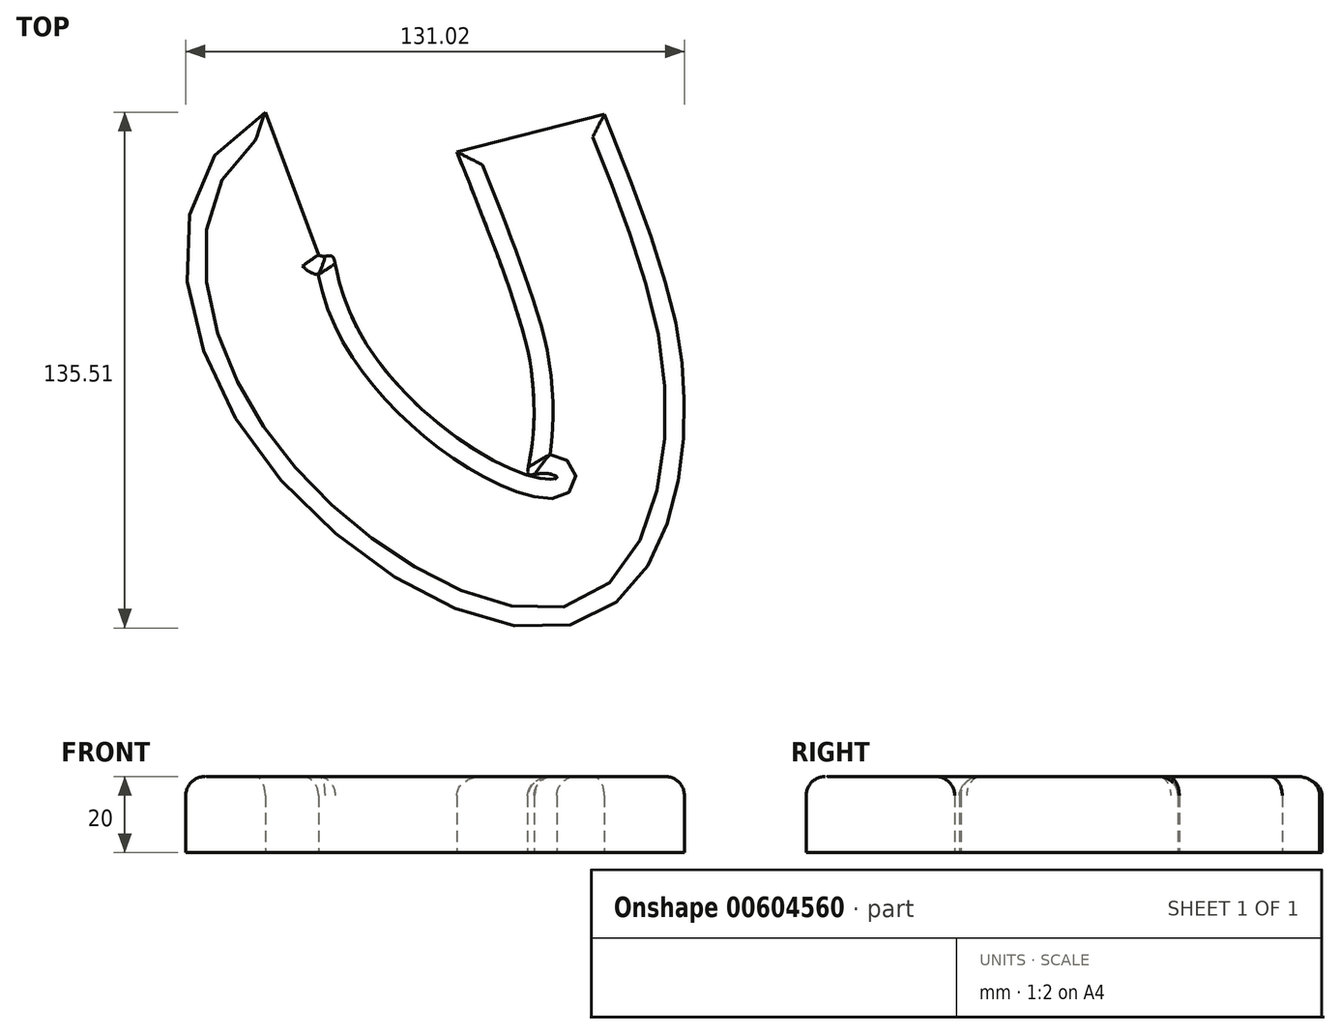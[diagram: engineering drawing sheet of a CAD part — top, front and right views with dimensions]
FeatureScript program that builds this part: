
annotation { "Feature Type Name" : "Feature", "Feature Type Description" : "" }
export const myFeature = defineFeature(function(context is Context, id is Id, definition is map)
    precondition{}
    {
        {
            var Q0;
            Q0=qCreatedBy(makeId("Front.planeOp"),FACE);
            var sketch = newSketch(context, id + "F0", { "sketchPlane" : qUnion([Q0])});
            skLineSegment(sketch, "E0.bottom", {"start": v(21.27, 4.94) * mm, "end": v(61.27, 4.94) * mm});
            skLineSegment(sketch, "E0.top", {"start": v(21.27, -15.06) * mm, "end": v(61.27, -15.06) * mm});
            skLineSegment(sketch, "E0.left", {"start": v(21.27, 4.94) * mm, "end": v(21.27, -15.06) * mm});
            skLineSegment(sketch, "E0.right", {"start": v(61.27, 4.94) * mm, "end": v(61.27, -15.06) * mm});
            skSolve(sketch);
        }
        {
            var Q0;
            Q0=qCreatedBy(makeId("Top.planeOp"),FACE);
            var sketch = newSketch(context, id + "F1", { "sketchPlane" : qUnion([Q0])});
            skFitSpline(sketch, "E1", {"points": [v(33.14, 61.3) * mm, v(49.3, 17.04) * mm, v(53.6, -5.31) * mm, v(50.47, -39.87) * mm, v(27.49, -63.27) * mm, v(-48.82, -12.21) * mm, v(-45.06, 56.16) * mm], "startDerivative": vector(151.19, -375.93) * mm, "endDerivative": vector(311.42, 166.25) * mm});
            skSolve(sketch);
        }
        {
            var Q0;
            Q0 = qSketchRegion(id + "F0", true);
            var Q1;
            Q1 = qConstructionFilter(qBodyType(qCreatedBy(id + "F1" ,EDGE), BodyType.WIRE), ConstructionObject.NO);
            sweep(context, id + "F2", {"profiles" : qUnion([Q0]), "path" : qUnion([Q1])});
        }
        {
            var Q0;
            Q0=makeQuery(id+"F2.opSweep","SWEPT_EDGE",EDGE,{"disambiguationData":[OSD([sQuery(id+"F0.wireOp",EDGE,"E0.bottom"),sQuery(id+"F0.wireOp",EDGE,"E0.right"),sQuery(id+"F1.wireOp",EDGE,"E1")])]});
            var Q1;
            Q1=makeQuery(id+"F2.opSweep","CAP_EDGE",EDGE,{"disambiguationData":[OSD([sQuery(id+"F0.wireOp",EDGE,"E0.bottom"),sQuery(id+"F1.wireOp",VERTEX,"E1.end")])],"isStart":false});
            var Q2;
            Q2=makeQuery(id+"F2.opSweep","SWEPT_EDGE",EDGE,{"disambiguationData":[OSD([sQuery(id+"F0.wireOp",EDGE,"E0.bottom"),sQuery(id+"F0.wireOp",EDGE,"E0.left"),sQuery(id+"F1.wireOp",EDGE,"E1")])]});
            var Q3;
            Q3=makeQuery(id+"F2.opSweep","CAP_EDGE",EDGE,{"disambiguationData":[OSD([sQuery(id+"F0.wireOp",EDGE,"E0.bottom"),sQuery(id+"F1.wireOp",VERTEX,"E1.start")])],"isStart":true});
            fillet(context, id + "F3", {"entities" : qUnion([Q0, Q1, Q2, Q3]), "radius" : 5 * mm, "tangentPropagation" : true, "allowEdgeOverflow" : false});
        }
    });
